# Revit family: Ribbeelement - TT
name_source: partatom
category: Structural Framing
units: mm (PartAtom-declared; Revit-internal decimal feet)

## family parameters
Always export as geometry = No
Always vertical = Yes
Cut with Voids When Loaded = No
Material for Model Behavior = Other
OmniClass Number = 23.25.30.11.14.14
OmniClass Title = Beams
Section Shape = Not Defined
Shared = No
Show family pre-cut in plan views = Yes

## types (11) — shared parameters
Bredde = 2392 mm  [stored 7.84777 ft]
CRH_RFA_TimeStamp_LastRelease = 20191107
Manufacturer = CRH Concrete
Pladebredde 1 = 1196 mm  [stored 3.92388 ft]
Pladebredde 2 = 1196 mm  [stored 3.92388 ft]
Pladetykkelse = 60 mm  [stored 0.19685 ft]
Pladetykkelse Standard = 60 mm  [stored 0.19685 ft]

## per-type parameters (varying)
| type | Højde | Højde Standard | Model | Ribbe CC Afstand | Show Sweep TT | Show Sweep TTD | Show Sweep TTD102 | Tværsnit TT | Tværsnit TTD |
| TTD 102 | 1020 mm  [stored 3.34646 ft] | 1020 mm  [stored 3.34646 ft] | TTD | 1250 mm  [stored 4.10105 ft] | No | No | Yes | No | Yes |
| TT 30 | 300 mm | 300 mm | TT | 1194 mm  [stored 3.91732 ft] | Yes | No | No | Yes | No |
| TT 40 | 400 mm  [stored 1.31234 ft] | 400 mm  [stored 1.31234 ft] | TT | 1194 mm  [stored 3.91732 ft] | Yes | No | No | Yes | No |
| TT 50 | 500 mm  [stored 1.64042 ft] | 500 mm  [stored 1.64042 ft] | TT | 1194 mm  [stored 3.91732 ft] | Yes | No | No | Yes | No |
| TT 60 | 600 mm | 600 mm | TT | 1194 mm  [stored 3.91732 ft] | Yes | No | No | Yes | No |
| TT 76 | 760 mm | 760 mm | TT | 1210 mm  [stored 3.96982 ft] | Yes | No | No | Yes | No |
| TTD 40 | 400 mm  [stored 1.31234 ft] | 400 mm  [stored 1.31234 ft] | TTD | 1214 mm  [stored 3.98294 ft] | No | Yes | No | No | Yes |
| TTD 50 | 500 mm  [stored 1.64042 ft] | 500 mm  [stored 1.64042 ft] | TTD | 1224 mm  [stored 4.01575 ft] | No | Yes | No | No | Yes |
| TTD 60 | 600 mm | 600 mm | TTD | 1234 mm  [stored 4.04856 ft] | No | Yes | No | No | Yes |
| TTD 76 | 760 mm | 760 mm | TTD | 1250 mm  [stored 4.10105 ft] | No | Yes | No | No | Yes |
| TTD 90 | 900 mm  [stored 2.95276 ft] | 900 mm  [stored 2.95276 ft] | TTD | 1250 mm  [stored 4.10105 ft] | No | Yes | No | No | Yes |

note: [stored X ft] marks values corroborated as IEEE doubles in the binary element streams (Revit-internal decimal feet)

## geometry (parser evidence)
native form markers: Sweep x7
no freeform markers — native parametric forms only
